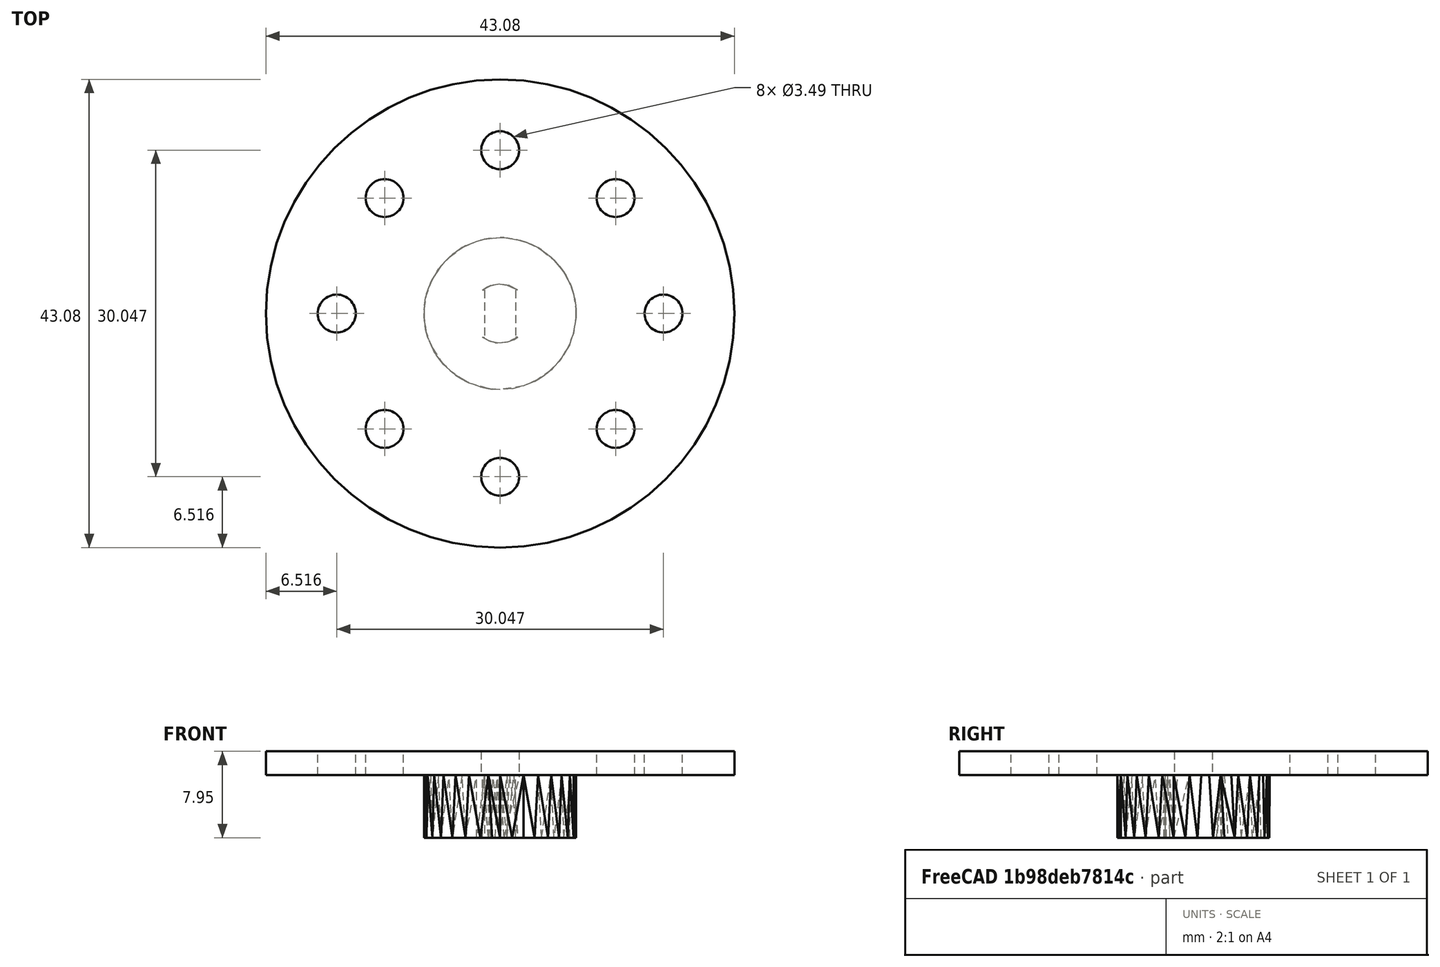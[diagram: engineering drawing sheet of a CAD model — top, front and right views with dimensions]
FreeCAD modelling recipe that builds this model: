
FCSTD DOCUMENT  (FreeCAD 0.19R24267 +148 (Git))
Label: FED disc 0.3mm
License: All rights reserved
LicenseURL: http://en.wikipedia.org/wiki/All_rights_reserved
objects: PartDesign::FeatureBase×2, Sketcher::SketchObject×2, PartDesign::Body×2, Part::Feature×1, Part::Extrusion×1, Part::MultiFuse×1, PartDesign::Pocket×1, PartDesign::PolarPattern×1
note: 12 computed .brp shape members not serialized (recipe doc carries the construction recipe); baked Part::Feature solids carry a one-line shape summary decoded from their .brp

FEATURE [Part::Feature] Body001001
  shape: bbox 13.96 x 14 x 5.751 mm, 148 faces (baked)
FEATURE [PartDesign::FeatureBase] BaseFeature003
  BaseFeature = -> Body001001
FEATURE [Sketcher::SketchObject] Sketch
  FullyConstrained = false
  MapMode = 5
  Placement = pos=(0,0,8.001) rot=(0,0,1;0rad)
  Support = -> [BaseFeature003]
  sketch-geometry (1):
    g0: Circle CenterX=0 CenterY=0 CenterZ=0 NormalX=0 NormalY=0 NormalZ=1 AngleXU=0 Radius=21.5397
  constraints (1):
    c: Coincident(g0,g-1)
FEATURE [PartDesign::Body] Body001002
  BaseFeature = -> Body001001
  Group = -> [BaseFeature003,Sketch]
  Origin = -> Origin003
  Tip = -> BaseFeature003
FEATURE [Part::Extrusion] Extrude
  Base = -> Sketch
  Dir = (0,0,1)
  DirMode = 2
  FaceMakerClass = Part::FaceMakerBullseye
  LengthFwd = 2.2
  LengthRev = 0
  Solid = true
  Symmetric = false
FEATURE [Part::MultiFuse] Fusion
  Shapes = -> [Body001002,Extrude]
FEATURE [PartDesign::FeatureBase] BaseFeature
  BaseFeature = -> Fusion
FEATURE [Sketcher::SketchObject] Sketch001
  FullyConstrained = false
  MapMode = 5
  Placement = pos=(0,0,10.201) rot=(0,0,1;0rad)
  Support = -> [BaseFeature]
  sketch-geometry (1):
    g0: Circle CenterX=0 CenterY=15.0237 CenterZ=0 NormalX=0 NormalY=0 NormalZ=1 AngleXU=0 Radius=1.74305
  constraints (1):
    c: PointOnObject(g0,g-2)
FEATURE [PartDesign::Pocket] Pocket
  BaseFeature = -> BaseFeature
  Length = 5
  Length2 = 100
  Profile = -> Sketch001
  Type = 0
FEATURE [PartDesign::PolarPattern] PolarPattern
  Angle = 360
  Axis = -> Sketch001 [N_Axis]
  BaseFeature = -> Pocket
  Occurrences = 8
  Originals = -> [Pocket]
FEATURE [PartDesign::Body] Body
  BaseFeature = -> Fusion
  Group = -> [BaseFeature,Sketch001,Pocket,PolarPattern]
  Origin = -> Origin
  Tip = -> PolarPattern
